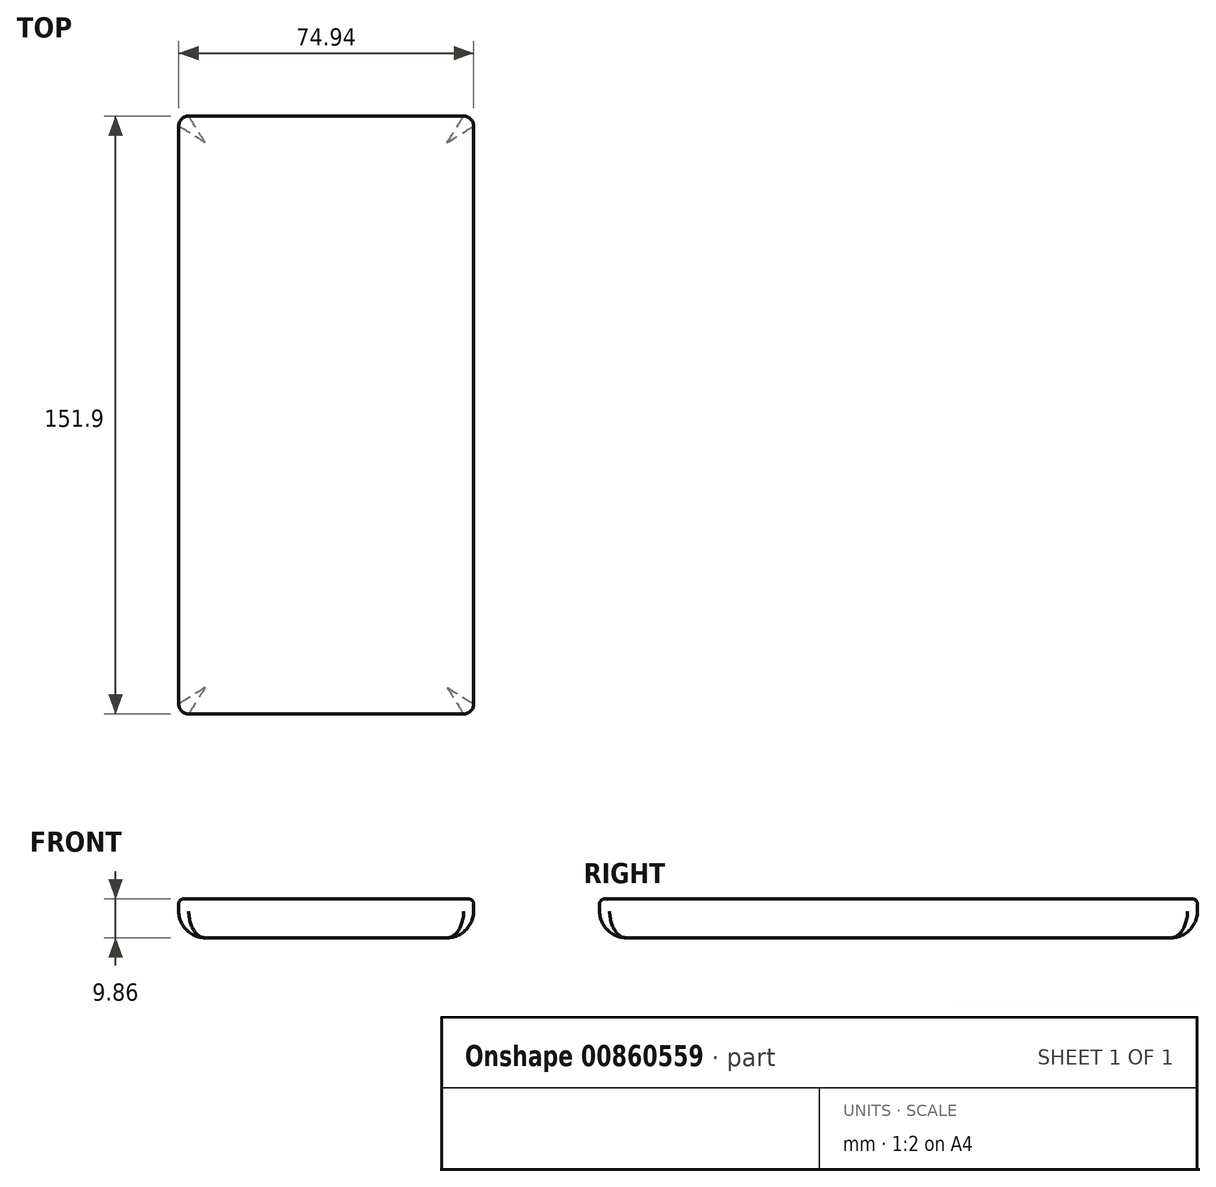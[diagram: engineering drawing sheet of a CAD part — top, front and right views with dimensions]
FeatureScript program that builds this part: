
annotation { "Feature Type Name" : "Feature", "Feature Type Description" : "" }
export const myFeature = defineFeature(function(context is Context, id is Id, definition is map)
    precondition{}
    {
        {
            var Q0;
            Q0=qCreatedBy(makeId("Top.planeOp"),FACE);
            var sketch = newSketch(context, id + "F0", { "sketchPlane" : qUnion([Q0])});
            skLineSegment(sketch, "E0.bottom", {"start": v(37.47, -75.95) * mm, "end": v(-37.46, -75.95) * mm});
            skLineSegment(sketch, "E0.top", {"start": v(37.46, 75.95) * mm, "end": v(-37.47, 75.95) * mm});
            skLineSegment(sketch, "E0.left", {"start": v(37.47, -75.95) * mm, "end": v(37.46, 75.95) * mm});
            skLineSegment(sketch, "E0.right", {"start": v(-37.46, -75.95) * mm, "end": v(-37.47, 75.95) * mm});
            skPoint(sketch, "E0.middle", {"position": v(0, 0) * mm});
            skSolve(sketch);
        }
        {
            var Q0;
            Q0=makeQuery(id+"F0.imprint","IMPRINT",FACE,{"disambiguationData":[TD([[makeQuery(id+"F0.imprint","IMPRINT",EDGE,{"derivedFrom":sQuery(id+"F0.wireOp",EDGE,"E0.bottom")}),-1.0]])]});
            extrude(context, id + "F1", {"entities" : qUnion([Q0]), "depth" : 9.86 * mm, "offsetDistance" : 25.4 * mm});
        }
        {
            var Q0;
            Q0=makeQuery(id+"F1.opExtrude","CAP_EDGE",EDGE,{"disambiguationData":[OSD([sQuery(id+"F0.wireOp",EDGE,"E0.bottom")])],"isStart":true});
            var Q1;
            Q1=makeQuery(id+"F1.opExtrude","CAP_EDGE",EDGE,{"disambiguationData":[OSD([sQuery(id+"F0.wireOp",EDGE,"E0.left")])],"isStart":true});
            var Q2;
            Q2=makeQuery(id+"F1.opExtrude","CAP_EDGE",EDGE,{"disambiguationData":[OSD([sQuery(id+"F0.wireOp",EDGE,"E0.right")])],"isStart":true});
            var Q3;
            Q3=makeQuery(id+"F1.opExtrude","CAP_EDGE",EDGE,{"disambiguationData":[OSD([sQuery(id+"F0.wireOp",EDGE,"E0.top")])],"isStart":true});
            fillet(context, id + "F2", {"entities" : qUnion([Q0, Q1, Q2, Q3]), "radius" : 6.75 * mm, "tangentPropagation" : true, "allowEdgeOverflow" : false});
        }
        {
            var Q0;
            Q0=makeQuery(id+"F1.opExtrude","CAP_EDGE",EDGE,{"disambiguationData":[OSD([sQuery(id+"F0.wireOp",EDGE,"E0.right")])],"isStart":false});
            var Q1;
            Q1=makeQuery(id+"F1.opExtrude","CAP_EDGE",EDGE,{"disambiguationData":[OSD([sQuery(id+"F0.wireOp",EDGE,"E0.top")])],"isStart":false});
            var Q2;
            Q2=makeQuery(id+"F1.opExtrude","CAP_EDGE",EDGE,{"disambiguationData":[OSD([sQuery(id+"F0.wireOp",EDGE,"E0.left")])],"isStart":false});
            var Q3;
            Q3=makeQuery(id+"F1.opExtrude","CAP_EDGE",EDGE,{"disambiguationData":[OSD([sQuery(id+"F0.wireOp",EDGE,"E0.bottom")])],"isStart":false});
            fillet(context, id + "F3", {"entities" : qUnion([Q0, Q1, Q2, Q3]), "radius" : 1.27 * mm, "tangentPropagation" : true, "allowEdgeOverflow" : false});
        }
        {
            var Q0;
            Q0=makeQuery(id+"F3.opFillet","BLEND_EDGE",EDGE,{"blendedFrom":[makeQuery(id+"F1.opExtrude","CAP_EDGE",EDGE,{"disambiguationData":[OSD([sQuery(id+"F0.wireOp",EDGE,"E0.top")])],"isStart":false}),makeQuery(id+"F1.opExtrude","CAP_EDGE",EDGE,{"disambiguationData":[OSD([sQuery(id+"F0.wireOp",EDGE,"E0.right")])],"isStart":false})],"blendedInto":[]});
            var Q1;
            Q1=makeQuery(id+"F3.opFillet","BLEND_EDGE",EDGE,{"blendedFrom":[makeQuery(id+"F1.opExtrude","CAP_EDGE",EDGE,{"disambiguationData":[OSD([sQuery(id+"F0.wireOp",EDGE,"E0.bottom")])],"isStart":false}),makeQuery(id+"F1.opExtrude","CAP_EDGE",EDGE,{"disambiguationData":[OSD([sQuery(id+"F0.wireOp",EDGE,"E0.right")])],"isStart":false})],"blendedInto":[]});
            var Q2;
            Q2=makeQuery(id+"F3.opFillet","BLEND_EDGE",EDGE,{"blendedFrom":[makeQuery(id+"F1.opExtrude","CAP_EDGE",EDGE,{"disambiguationData":[OSD([sQuery(id+"F0.wireOp",EDGE,"E0.bottom")])],"isStart":false}),makeQuery(id+"F1.opExtrude","CAP_EDGE",EDGE,{"disambiguationData":[OSD([sQuery(id+"F0.wireOp",EDGE,"E0.left")])],"isStart":false})],"blendedInto":[]});
            var Q3;
            Q3=makeQuery(id+"F3.opFillet","BLEND_EDGE",EDGE,{"blendedFrom":[makeQuery(id+"F1.opExtrude","CAP_EDGE",EDGE,{"disambiguationData":[OSD([sQuery(id+"F0.wireOp",EDGE,"E0.top")])],"isStart":false}),makeQuery(id+"F1.opExtrude","CAP_EDGE",EDGE,{"disambiguationData":[OSD([sQuery(id+"F0.wireOp",EDGE,"E0.left")])],"isStart":false})],"blendedInto":[]});
            fillet(context, id + "F4", {"entities" : qUnion([Q0, Q1, Q2, Q3]), "radius" : 2.54 * mm, "tangentPropagation" : true, "allowEdgeOverflow" : false});
        }
    });
